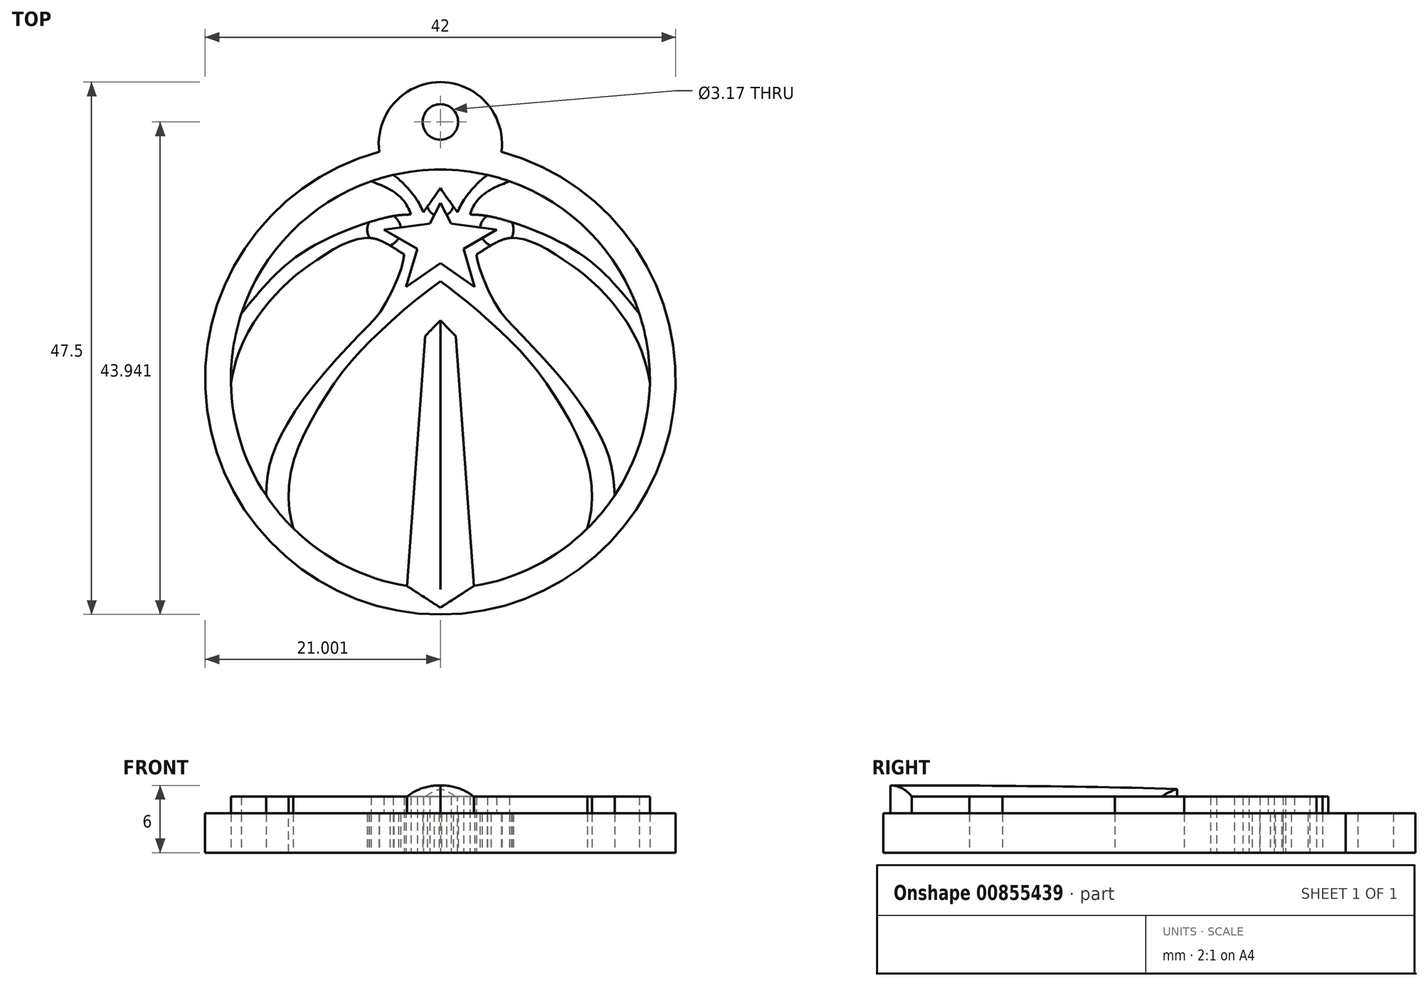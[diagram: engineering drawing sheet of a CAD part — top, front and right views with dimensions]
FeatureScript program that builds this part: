
annotation { "Feature Type Name" : "Feature", "Feature Type Description" : "" }
export const myFeature = defineFeature(function(context is Context, id is Id, definition is map)
    precondition{}
    {
        {
            var Q0;
            Q0=qCreatedBy(makeId("Top.planeOp"),FACE);
            var sketch = newSketch(context, id + "F0", { "sketchPlane" : qUnion([Q0])});
            skCircle(sketch, "E0", {"center": v(-5.17, -2.11) * mm, "radius": 21 * mm});
            skArc(sketch, "E1", {"start": v(-2.18, -20.57) * mm, "mid": v(-5.17, 16.59) * mm, "end": v(-8.15, -20.57) * mm});
            skLineSegment(sketch, "E2", {"start": v(-8.15, -20.57) * mm, "end": v(-5.17, -22.5) * mm});
            skLineSegment(sketch, "E3", {"start": v(-8.15, -20.57) * mm, "end": v(-6.53, 1.73) * mm});
            skLineSegment(sketch, "E4", {"start": v(-6.53, 1.73) * mm, "end": v(-5.17, 3.12) * mm});
            skFitSpline(sketch, "E5", {"points": [v(-18.3, -15.43) * mm, v(-18.7, -13.28) * mm, v(-18.33, -9.6) * mm, v(-16.56, -5.57) * mm, v(-13.88, -1.44) * mm, v(-10.93, 1.78) * mm, v(-7.35, 4.95) * mm, v(-5.17, 6.63) * mm], "startDerivative": vector(-4.67, 18.35) * mm, "endDerivative": vector(16.75, 12.42) * mm});
            skFitSpline(sketch, "E6", {"points": [v(-20.73, -12.48) * mm, v(-20.46, -10.02) * mm, v(-19.46, -7.25) * mm, v(-16.38, -2.58) * mm, v(-11.98, 2.28) * mm, v(-10.25, 4.32) * mm, v(-8.66, 7.77) * mm, v(-8.4, 9) * mm], "startDerivative": vector(1.2, 20.25) * mm, "endDerivative": vector(1.72, 11.89) * mm});
            skFitSpline(sketch, "E7", {"points": [v(-8.4, 9) * mm, v(-9.3, 9.58) * mm, v(-10.75, 10.33) * mm, v(-11.95, 10.47) * mm, v(-13.88, 9.9) * mm, v(-16.62, 8.22) * mm, v(-18.73, 6.6) * mm, v(-21.6, 3.3) * mm, v(-23.31, -0.15) * mm, v(-23.87, -2.46) * mm], "startDerivative": vector(-11.06, 7.5) * mm, "endDerivative": vector(-3.57, -19.95) * mm});
            skFitSpline(sketch, "E8", {"points": [v(-22.93, 3.73) * mm, v(-20.52, 6.57) * mm, v(-16.56, 9.74) * mm, v(-9.93, 12.33) * mm, v(-7.8, 12.58) * mm], "startDerivative": vector(9.8, 12.32) * mm, "endDerivative": vector(10.15, 0.31) * mm});
            skFitSpline(sketch, "E9", {"points": [v(-7.8, 12.58) * mm, v(-8.23, 13.5) * mm, v(-9.14, 14.46) * mm, v(-10.36, 15.14) * mm, v(-11.35, 15.54) * mm], "startDerivative": vector(-1.53, 4.05) * mm, "endDerivative": vector(-4.05, 1.5) * mm});
            skFitSpline(sketch, "E10", {"points": [v(-9.38, 16.1) * mm, v(-8.62, 15.48) * mm, v(-7.35, 14) * mm, v(-6.69, 12.78) * mm], "startDerivative": vector(2.55, -1.84) * mm, "endDerivative": vector(1.65, -3.56) * mm});
            skFitSpline(sketch, "E11", {"points": [v(-6.69, 12.78) * mm, v(-5.87, 13.92) * mm, v(-5.17, 14.94) * mm], "startDerivative": vector(1.62, 2.23) * mm, "endDerivative": vector(1.42, 2.08) * mm});
            skLineSegment(sketch, "E12", {"start": v(-5.17, 13.6) * mm, "end": v(-6.13, 11.76) * mm});
            skLineSegment(sketch, "E13", {"start": v(-6.13, 11.76) * mm, "end": v(-10.2, 11.22) * mm});
            skLineSegment(sketch, "E14", {"start": v(-10.2, 11.22) * mm, "end": v(-7.23, 9.52) * mm});
            skLineSegment(sketch, "E15", {"start": v(-7.23, 9.52) * mm, "end": v(-8.23, 6.1) * mm});
            skLineSegment(sketch, "E16", {"start": v(-8.23, 6.1) * mm, "end": v(-5.17, 8.23) * mm});
            skArc(sketch, "E17", {"start": v(-5.28, 13.39) * mm, "mid": v(-5.22, 13.39) * mm, "end": v(-5.17, 13.39) * mm});
            skArc(sketch, "E18.trimOffspring", {"start": v(0.28, 18.17) * mm, "mid": v(-5.17, 24.39) * mm, "end": v(-10.62, 18.17) * mm});
            skCircle(sketch, "E19", {"center": v(-5.17, 20.83) * mm, "radius": 1.59 * mm});
            skFitSpline(sketch, "E20.MirrorCS", {"points": [v(-0.96, 16.1) * mm, v(-1.72, 15.48) * mm, v(-2.99, 14) * mm, v(-3.65, 12.78) * mm], "startDerivative": vector(-2.55, -1.84) * mm, "endDerivative": vector(-1.65, -3.56) * mm});
            skFitSpline(sketch, "E21.MirrorCS", {"points": [v(-3.65, 12.78) * mm, v(-4.47, 13.92) * mm, v(-5.17, 14.94) * mm], "startDerivative": vector(-1.62, 2.23) * mm, "endDerivative": vector(-1.42, 2.08) * mm});
            skLineSegment(sketch, "E22.MirrorCS", {"start": v(-5.17, 13.6) * mm, "end": v(-4.21, 11.76) * mm});
            skLineSegment(sketch, "E23.MirrorCS", {"start": v(-4.21, 11.76) * mm, "end": v(-0.14, 11.22) * mm});
            skLineSegment(sketch, "E24.MirrorCS", {"start": v(-0.14, 11.22) * mm, "end": v(-3.1, 9.52) * mm});
            skLineSegment(sketch, "E25.MirrorCS", {"start": v(-3.1, 9.52) * mm, "end": v(-2.1, 6.1) * mm});
            skLineSegment(sketch, "E26.MirrorCS", {"start": v(-2.1, 6.1) * mm, "end": v(-5.17, 8.23) * mm});
            skFitSpline(sketch, "E27.MirrorCS", {"points": [v(-2.54, 12.58) * mm, v(-2.1, 13.5) * mm, v(-1.2, 14.46) * mm, v(0.02, 15.14) * mm, v(1, 15.54) * mm], "startDerivative": vector(1.53, 4.05) * mm, "endDerivative": vector(4.05, 1.5) * mm});
            skFitSpline(sketch, "E28.MirrorCS", {"points": [v(12.6, 3.73) * mm, v(10.19, 6.57) * mm, v(6.22, 9.74) * mm, v(-0.4, 12.33) * mm, v(-2.54, 12.58) * mm], "startDerivative": vector(-9.8, 12.32) * mm, "endDerivative": vector(-10.15, 0.31) * mm});
            skFitSpline(sketch, "E29.MirrorCS", {"points": [v(-1.95, 9) * mm, v(-1.04, 9.58) * mm, v(0.41, 10.33) * mm, v(1.61, 10.47) * mm, v(3.54, 9.9) * mm, v(6.28, 8.22) * mm, v(8.4, 6.6) * mm, v(11.25, 3.3) * mm, v(12.98, -0.15) * mm, v(13.53, -2.46) * mm], "startDerivative": vector(11.06, 7.5) * mm, "endDerivative": vector(3.57, -19.95) * mm});
            skFitSpline(sketch, "E30.MirrorCS", {"points": [v(10.4, -12.48) * mm, v(10.12, -10.02) * mm, v(9.12, -7.25) * mm, v(6.04, -2.58) * mm, v(1.64, 2.28) * mm, v(-0.09, 4.32) * mm, v(-1.67, 7.77) * mm, v(-1.95, 9) * mm], "startDerivative": vector(-1.2, 20.25) * mm, "endDerivative": vector(-1.72, 11.89) * mm});
            skFitSpline(sketch, "E31.MirrorCS", {"points": [v(7.96, -15.43) * mm, v(8.35, -13.28) * mm, v(7.99, -9.6) * mm, v(6.22, -5.57) * mm, v(3.54, -1.44) * mm, v(0.6, 1.78) * mm, v(-2.99, 4.95) * mm, v(-5.17, 6.63) * mm], "startDerivative": vector(4.67, 18.35) * mm, "endDerivative": vector(-16.75, 12.42) * mm});
            skLineSegment(sketch, "E32.MirrorCS", {"start": v(-2.18, -20.57) * mm, "end": v(-3.8, 1.73) * mm});
            skLineSegment(sketch, "E33.MirrorCS", {"start": v(-3.8, 1.73) * mm, "end": v(-5.17, 3.12) * mm});
            skLineSegment(sketch, "E34.MirrorCS", {"start": v(-2.18, -20.57) * mm, "end": v(-5.17, -22.5) * mm});
            skCircle(sketch, "E35", {"center": v(-5.17, 13.6) * mm, "radius": 1.2 * mm});
            skCircle(sketch, "E36", {"center": v(-0.14, 11.22) * mm, "radius": 1.5 * mm});
            skCircle(sketch, "E37", {"center": v(-10.2, 11.22) * mm, "radius": 1.5 * mm});
            skSolve(sketch);
        }
        {
            var Q0;
            {var subQ0=sQuery(id+"F0.wireOp",EDGE,"E18.trimOffspring");Q0=makeQuery(id+"F0.imprint","IMPRINT",FACE,{"disambiguationData":[TD([[makeQuery(id+"F0.imprint","IMPRINT",EDGE,{"derivedFrom":subQ0}),1.0]])]});}
            var Q1;
            {var subQ18=sQuery(id+"F0.wireOp",EDGE,"E2");Q1=makeQuery(id+"F0.imprint","IMPRINT",FACE,{"disambiguationData":[TD([[makeQuery(id+"F0.imprint","IMPRINT",EDGE,{"derivedFrom":subQ18}),-1.0]])]});}
            var Q2;
            {var subQ3=sQuery(id+"F0.wireOp",EDGE,"E37");var subQ9=sQuery(id+"F0.wireOp",EDGE,"E7");var subQ11=makeQuery(id+"F0.imprint","INTERSECT",VERTEX,{"disambiguationData":[OD(0.0)],"derivedFrom":[subQ9,subQ3]});Q2=makeQuery(id+"F0.imprint","IMPRINT",FACE,{"disambiguationData":[TD([[makeQuery(id+"F0.imprint","IMPRINT",EDGE,{"disambiguationData":[TD([[subQ11,-1.0]])],"derivedFrom":subQ9}),-1.0]])]});}
            var Q3;
            {var subQ0=sQuery(id+"F0.wireOp",EDGE,"E12");var subQ1=makeQuery(id+"F0.imprint","IMPRINT",VERTEX,{"derivedFrom":subQ0});Q3=makeQuery(id+"F0.imprint","IMPRINT",FACE,{"disambiguationData":[TD([[makeQuery(id+"F0.imprint","IMPRINT",EDGE,{"disambiguationData":[TD([[subQ1,1.0]])],"derivedFrom":subQ0}),-1.0]])]});}
            var Q4;
            {var subQ4=sQuery(id+"F0.wireOp",EDGE,"E24.MirrorCS");var subQ5=sQuery(id+"F0.wireOp",EDGE,"E23.MirrorCS");var subQ6=makeQuery(id+"F0.imprint","INTERSECT",VERTEX,{"derivedFrom":[subQ5,subQ4]});Q4=makeQuery(id+"F0.imprint","IMPRINT",FACE,{"disambiguationData":[TD([[makeQuery(id+"F0.imprint","IMPRINT",EDGE,{"disambiguationData":[TD([[subQ6,1.0]])],"derivedFrom":subQ5}),1.0]])]});}
            extrude(context, id + "F1", {"entities" : qUnion([Q0, Q1, Q2, Q3, Q4]), "depth" : 3.5 * mm, "offsetDistance" : 25 * mm});
        }
        {
            var Q0;
            {var subQ0=sQuery(id+"F0.wireOp",EDGE,"E3");Q0=makeQuery(id+"F0.imprint","IMPRINT",FACE,{"disambiguationData":[TD([[makeQuery(id+"F0.imprint","IMPRINT",EDGE,{"derivedFrom":subQ0}),1.0]])]});}
            var Q1;
            {var subQ0=sQuery(id+"F0.wireOp",EDGE,"E29.MirrorCS");Q1=makeQuery(id+"F0.imprint","IMPRINT",FACE,{"disambiguationData":[TD([[makeQuery(id+"F0.imprint","IMPRINT",EDGE,{"derivedFrom":subQ0}),-1.0]])]});}
            var Q2;
            {var subQ0=sQuery(id+"F0.wireOp",EDGE,"E27.MirrorCS");Q2=makeQuery(id+"F0.imprint","IMPRINT",FACE,{"disambiguationData":[TD([[makeQuery(id+"F0.imprint","IMPRINT",EDGE,{"derivedFrom":subQ0}),-1.0]])]});}
            var Q3;
            {var subQ1=sQuery(id+"F0.wireOp",EDGE,"E10");Q3=makeQuery(id+"F0.imprint","IMPRINT",FACE,{"disambiguationData":[TD([[makeQuery(id+"F0.imprint","IMPRINT",EDGE,{"derivedFrom":subQ1}),1.0]])]});}
            var Q4;
            {var subQ0=sQuery(id+"F0.wireOp",EDGE,"E8");Q4=makeQuery(id+"F0.imprint","IMPRINT",FACE,{"disambiguationData":[TD([[makeQuery(id+"F0.imprint","IMPRINT",EDGE,{"derivedFrom":subQ0}),1.0]])]});}
            var Q5;
            {var subQ0=sQuery(id+"F0.wireOp",EDGE,"E6");Q5=makeQuery(id+"F0.imprint","IMPRINT",FACE,{"disambiguationData":[TD([[makeQuery(id+"F0.imprint","IMPRINT",EDGE,{"derivedFrom":subQ0}),1.0]])]});}
            var Q6;
            {var subQ0=sQuery(id+"F0.wireOp",EDGE,"E37");var subQ1=sQuery(id+"F0.wireOp",EDGE,"E8");var subQ2=makeQuery(id+"F0.imprint","INTERSECT",VERTEX,{"disambiguationData":[OD(0.0)],"derivedFrom":[subQ1,subQ0]});Q6=makeQuery(id+"F0.imprint","IMPRINT",FACE,{"disambiguationData":[TD([[makeQuery(id+"F0.imprint","IMPRINT",EDGE,{"disambiguationData":[TD([[subQ2,-1.0]])],"derivedFrom":subQ1}),1.0]])]});}
            var Q7;
            {var subQ0=sQuery(id+"F0.wireOp",EDGE,"E37");var subQ1=sQuery(id+"F0.wireOp",EDGE,"E7");var subQ2=makeQuery(id+"F0.imprint","INTERSECT",VERTEX,{"disambiguationData":[OD(0.0)],"derivedFrom":[subQ1,subQ0]});Q7=makeQuery(id+"F0.imprint","IMPRINT",FACE,{"disambiguationData":[TD([[makeQuery(id+"F0.imprint","IMPRINT",EDGE,{"disambiguationData":[TD([[subQ2,-1.0]])],"derivedFrom":subQ1}),1.0]])]});}
            var Q8;
            {var subQ0=sQuery(id+"F0.wireOp",EDGE,"E35");var subQ1=sQuery(id+"F0.wireOp",EDGE,"E11");var subQ2=makeQuery(id+"F0.imprint","INTERSECT",VERTEX,{"disambiguationData":[OD(0.0)],"derivedFrom":[subQ1,subQ0]});Q8=makeQuery(id+"F0.imprint","IMPRINT",FACE,{"disambiguationData":[TD([[makeQuery(id+"F0.imprint","IMPRINT",EDGE,{"disambiguationData":[TD([[subQ2,-1.0]])],"derivedFrom":subQ1}),1.0]])]});}
            var Q9;
            {var subQ0=sQuery(id+"F0.wireOp",EDGE,"E35");var subQ1=sQuery(id+"F0.wireOp",EDGE,"E21.MirrorCS");var subQ2=makeQuery(id+"F0.imprint","INTERSECT",VERTEX,{"disambiguationData":[OD(0.0)],"derivedFrom":[subQ1,subQ0]});Q9=makeQuery(id+"F0.imprint","IMPRINT",FACE,{"disambiguationData":[TD([[makeQuery(id+"F0.imprint","IMPRINT",EDGE,{"disambiguationData":[TD([[subQ2,-1.0]])],"derivedFrom":subQ1}),-1.0]])]});}
            var Q10;
            {var subQ0=sQuery(id+"F0.wireOp",EDGE,"E36");var subQ1=sQuery(id+"F0.wireOp",EDGE,"E28.MirrorCS");var subQ2=makeQuery(id+"F0.imprint","INTERSECT",VERTEX,{"disambiguationData":[OD(0.0)],"derivedFrom":[subQ1,subQ0]});Q10=makeQuery(id+"F0.imprint","IMPRINT",FACE,{"disambiguationData":[TD([[makeQuery(id+"F0.imprint","IMPRINT",EDGE,{"disambiguationData":[TD([[subQ2,-1.0]])],"derivedFrom":subQ1}),-1.0]])]});}
            var Q11;
            {var subQ0=sQuery(id+"F0.wireOp",EDGE,"E36");var subQ1=sQuery(id+"F0.wireOp",EDGE,"E29.MirrorCS");var subQ2=makeQuery(id+"F0.imprint","INTERSECT",VERTEX,{"disambiguationData":[OD(0.0)],"derivedFrom":[subQ1,subQ0]});Q11=makeQuery(id+"F0.imprint","IMPRINT",FACE,{"disambiguationData":[TD([[makeQuery(id+"F0.imprint","IMPRINT",EDGE,{"disambiguationData":[TD([[subQ2,-1.0]])],"derivedFrom":subQ1}),-1.0]])]});}
            extrude(context, id + "F2", {"entities" : qUnion([Q0, Q1, Q2, Q3, Q4, Q5, Q6, Q7, Q8, Q9, Q10, Q11]), "operationType" : NewBodyOperationType.ADD, "depth" : 5 * mm, "offsetDistance" : 25 * mm});
        }
        {
            var Q0;
            {var subQ14=sQuery(id+"F0.wireOp",EDGE,"E15");Q0=makeQuery(id+"F0.imprint","IMPRINT",FACE,{"disambiguationData":[TD([[makeQuery(id+"F0.imprint","IMPRINT",EDGE,{"derivedFrom":subQ14}),1.0]])]});}
            var Q1;
            {var subQ0=sQuery(id+"F0.wireOp",EDGE,"E14");var subQ1=sQuery(id+"F0.wireOp",EDGE,"E13");var subQ2=makeQuery(id+"F0.imprint","INTERSECT",VERTEX,{"derivedFrom":[subQ1,subQ0]});Q1=makeQuery(id+"F0.imprint","IMPRINT",FACE,{"disambiguationData":[TD([[makeQuery(id+"F0.imprint","IMPRINT",EDGE,{"disambiguationData":[TD([[subQ2,1.0]])],"derivedFrom":subQ1}),1.0]])]});}
            var Q2;
            {var subQ1=sQuery(id+"F0.wireOp",EDGE,"E12");var subQ3=makeQuery(id+"F0.imprint","IMPRINT",VERTEX,{"derivedFrom":subQ1});Q2=makeQuery(id+"F0.imprint","IMPRINT",FACE,{"disambiguationData":[TD([[makeQuery(id+"F0.imprint","IMPRINT",EDGE,{"disambiguationData":[TD([[subQ3,1.0]])],"derivedFrom":subQ1}),1.0]])]});}
            var Q3;
            {var subQ0=sQuery(id+"F0.wireOp",EDGE,"E24.MirrorCS");var subQ1=sQuery(id+"F0.wireOp",EDGE,"E23.MirrorCS");var subQ2=makeQuery(id+"F0.imprint","INTERSECT",VERTEX,{"derivedFrom":[subQ1,subQ0]});Q3=makeQuery(id+"F0.imprint","IMPRINT",FACE,{"disambiguationData":[TD([[makeQuery(id+"F0.imprint","IMPRINT",EDGE,{"disambiguationData":[TD([[subQ2,1.0]])],"derivedFrom":subQ1}),-1.0]])]});}
            extrude(context, id + "F3", {"entities" : qUnion([Q0, Q1, Q2, Q3]), "operationType" : NewBodyOperationType.ADD, "depth" : 5 * mm, "offsetDistance" : 25 * mm});
        }
        {
            var Q0;
            Q0=makeQuery(id+"F0.imprint","IMPRINT",FACE,{"disambiguationData":[TD([[makeQuery(id+"F0.imprint","IMPRINT",EDGE,{"derivedFrom":sQuery(id+"F0.wireOp",EDGE,"E2")}),1.0]])]});
            extrude(context, id + "F4", {"entities" : qUnion([Q0]), "operationType" : NewBodyOperationType.ADD, "depth" : 6 * mm, "offsetDistance" : 25 * mm});
        }
        {
            var Q0;
            Q0=makeQuery(id+"F4.opExtrude","CAP_EDGE",EDGE,{"disambiguationData":[OSD([sQuery(id+"F0.wireOp",EDGE,"E3")])],"isStart":false});
            var Q1;
            Q1=makeQuery(id+"F4.opExtrude","CAP_EDGE",EDGE,{"disambiguationData":[OSD([sQuery(id+"F0.wireOp",EDGE,"E32.MirrorCS")])],"isStart":false});
            fillet(context, id + "F5", {"entities" : qUnion([Q0, Q1]), "radius" : 5 * mm, "tangentPropagation" : true, "allowEdgeOverflow" : false});
        }
    });
